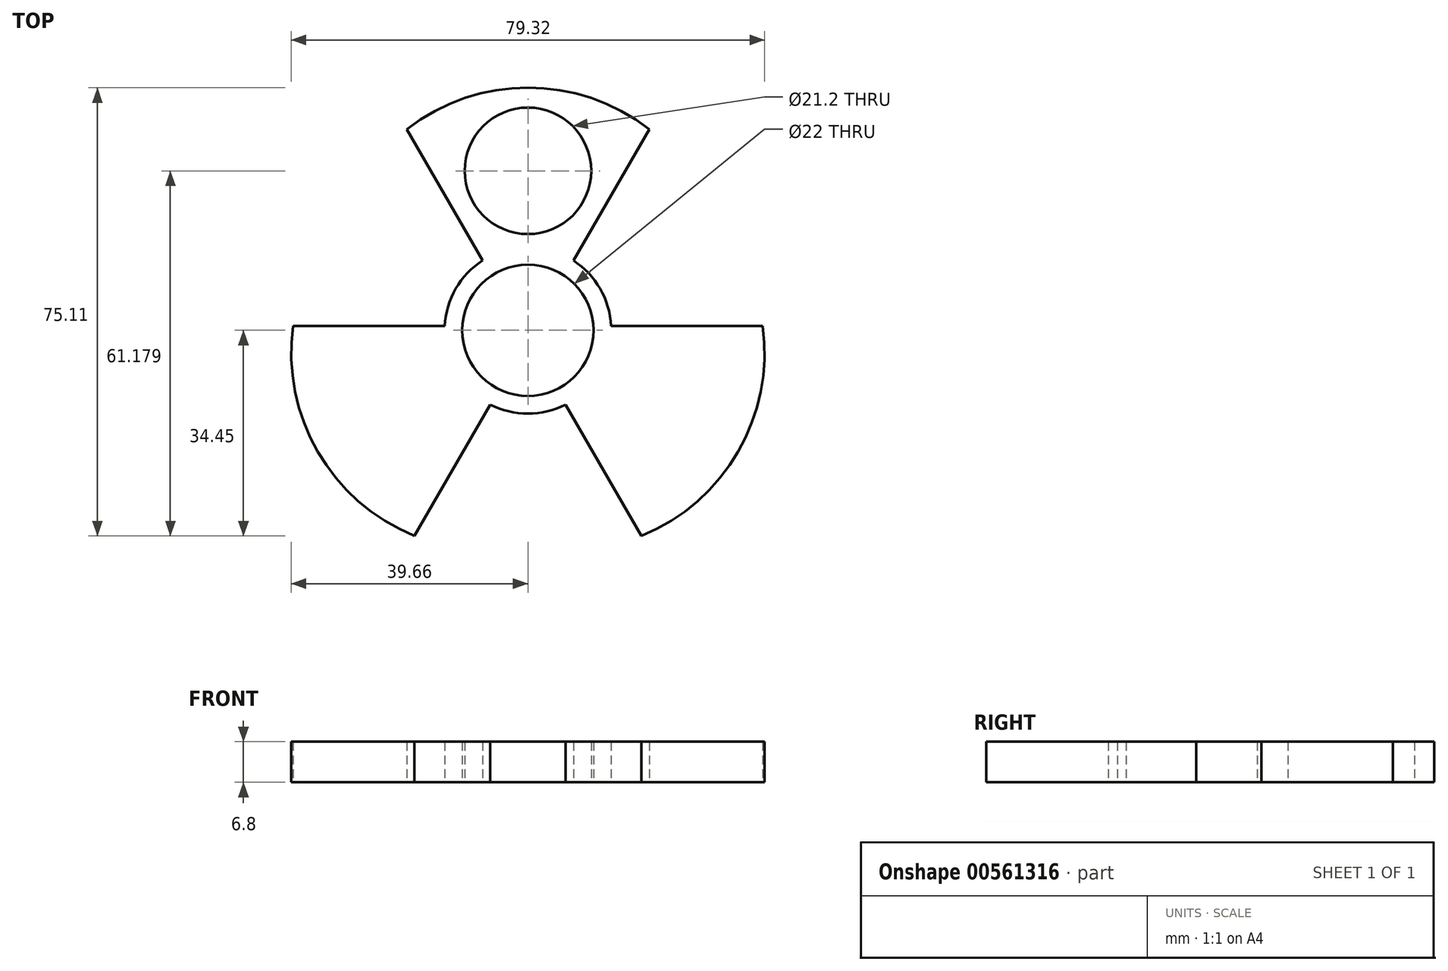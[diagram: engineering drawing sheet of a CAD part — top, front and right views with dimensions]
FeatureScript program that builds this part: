
annotation { "Feature Type Name" : "Feature", "Feature Type Description" : "" }
export const myFeature = defineFeature(function(context is Context, id is Id, definition is map)
    precondition{}
    {
        {
            var Q0;
            Q0=qCreatedBy(makeId("Top.planeOp"),FACE);
            var sketch = newSketch(context, id + "F0", { "sketchPlane" : qUnion([Q0])});
            skCircle(sketch, "E0", {"center": v(0, 0) * mm, "radius": 11 * mm});
            skCircle(sketch, "E1", {"center": v(0, 0) * mm, "radius": 13.97 * mm});
            skLineSegment(sketch, "E2", {"start": v(-7.62, 11.7) * mm, "end": v(-20.32, 33.7) * mm});
            skLineSegment(sketch, "E3", {"start": v(20.32, 33.7) * mm, "end": v(7.62, 11.7) * mm});
            skArc(sketch, "E4", {"start": v(20.32, 33.7) * mm, "mid": v(0, 40.66) * mm, "end": v(-20.32, 33.7) * mm});
            skArc(sketch, "E5.1.0", {"start": v(-39.35, 0.74) * mm, "mid": v(-35.21, -20.33) * mm, "end": v(-19.03, -34.45) * mm});
            skLineSegment(sketch, "E5.1.1", {"start": v(-39.35, 0.74) * mm, "end": v(-13.95, 0.74) * mm});
            skLineSegment(sketch, "E5.1.2", {"start": v(-6.33, -12.45) * mm, "end": v(-19.03, -34.45) * mm});
            skArc(sketch, "E5.2.0", {"start": v(19.03, -34.45) * mm, "mid": v(35.21, -20.33) * mm, "end": v(39.35, 0.74) * mm});
            skLineSegment(sketch, "E5.2.1", {"start": v(19.03, -34.45) * mm, "end": v(6.33, -12.45) * mm});
            skLineSegment(sketch, "E5.2.2", {"start": v(13.95, 0.74) * mm, "end": v(39.35, 0.74) * mm});
            skCircle(sketch, "E6", {"center": v(0, 26.73) * mm, "radius": 10.6 * mm});
            skSolve(sketch);
        }
        {
            var Q0;
            Q0 = qSketchRegion(id + "F0", true);
            extrude(context, id + "F1", {"entities" : qUnion([Q0]), "depth" : 6.8 * mm, "offsetDistance" : 25.4 * mm});
        }
    });
